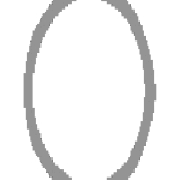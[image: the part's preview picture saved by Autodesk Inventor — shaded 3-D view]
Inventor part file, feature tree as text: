
AUTODESK INVENTOR PART (.ipt)
format: ipt  version: 2021 (Build 250183000, 183)  size: 162,816 bytes
history: native  units: in
note: dims shown in document units (in); Inventor stores cm internally (conversion verified against a paired STEP export)
features: other x5, sketch x2, sweep x1, plane x1
ambient origin geometry x8: Origin, YZ Plane, XZ Plane, XY Plane, X Axis, Y Axis, Z Axis, Center Point
bodies: Solid1 (feature_tree), Body (feature_tree)
feature tree (9):
  other  "Driven Length"
  other  "Frame Generator"
  other  "Start Plane"
  other  "End Plane"
  sweep  "Sweep Path"
  other  "Orientation Work Plane"
  sketch  "Sketch2"  dims[d0=1.0in d1=0.065in]
  plane  "Work Plane3"
  sketch  "Sketch3"  dims[d2=16.5001in d4=-0.0in d5=16.5001in d8=90.0deg d9=16.5001in d10=0.0in d11=0.0in]
